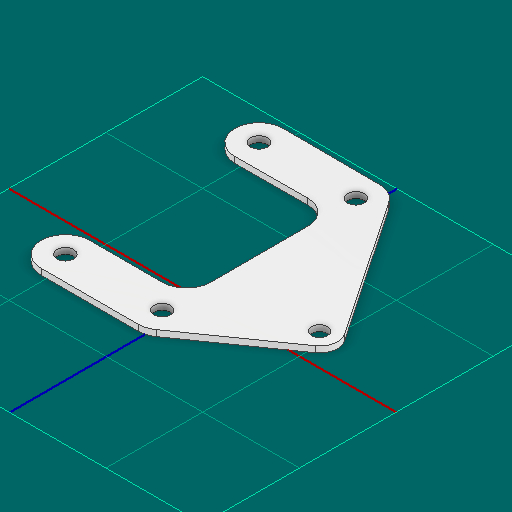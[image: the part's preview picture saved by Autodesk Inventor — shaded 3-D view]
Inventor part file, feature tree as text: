
AUTODESK INVENTOR PART (.ipt)
format: ipt  version: 2025 (Build 290162000, 162)  size: 134,144 bytes
history: native  units: in
note: dims shown in document units (in); Inventor stores cm internally (conversion verified against a paired STEP export)
features: other x3, sketch x1
ambient origin geometry x8: Origin, YZ Plane, XZ Plane, XY Plane, X Axis, Y Axis, Z Axis, Center Point
bodies: Solid1 (feature_tree)
feature tree (4):
  other  "gusset.ipt"
  other  "Solid1::gusset.ipt"
  other  "TaggingFeature1"
  sketch  "Sketch1"  dims[d0=0.3937in]
